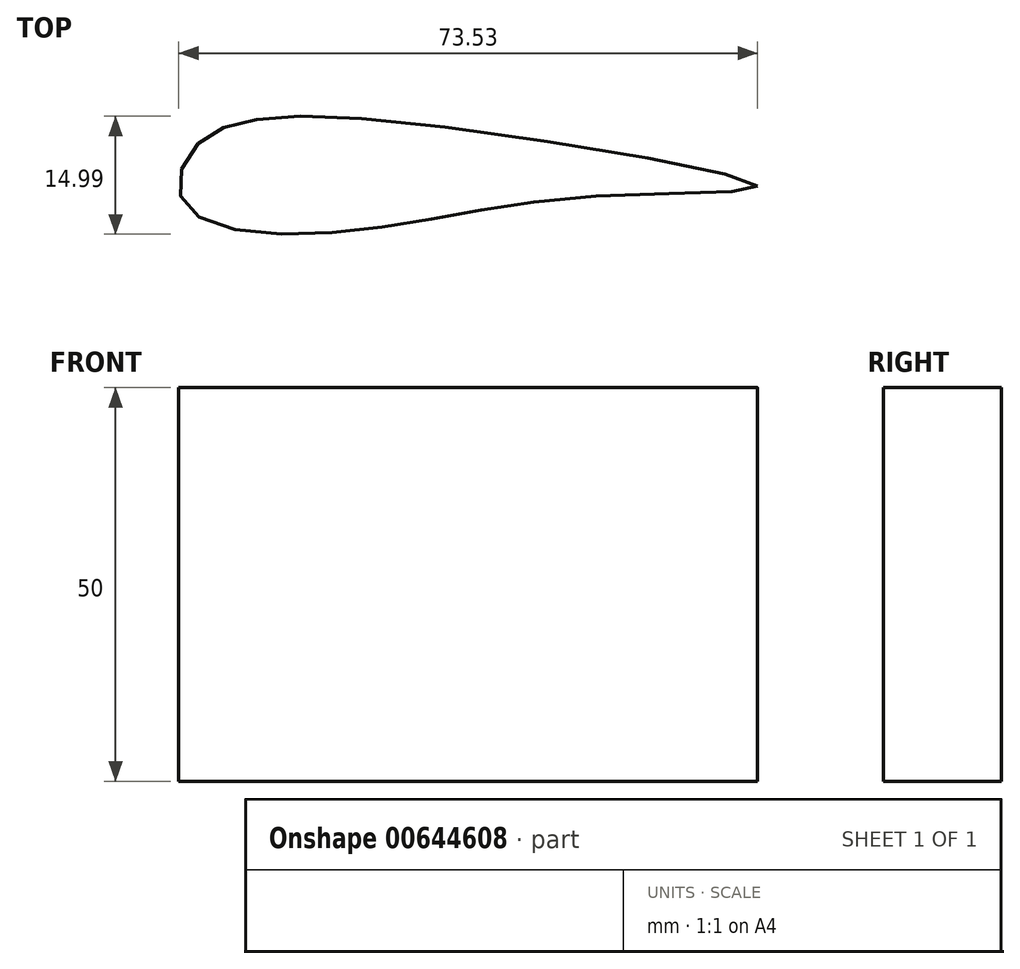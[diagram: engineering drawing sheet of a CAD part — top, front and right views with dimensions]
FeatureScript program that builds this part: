
annotation { "Feature Type Name" : "Feature", "Feature Type Description" : "" }
export const myFeature = defineFeature(function(context is Context, id is Id, definition is map)
    precondition{}
    {
        {
            var Q0;
            Q0=qCreatedBy(makeId("Top.planeOp"),FACE);
            var sketch = newSketch(context, id + "F0", { "sketchPlane" : qUnion([Q0])});
            skFitSpline(sketch, "E0", {"points": [v(73.53, 3.05) * mm, v(29.86, 10.98) * mm, v(8.21, 11.16) * mm, v(2.43, 8.36) * mm, v(0, 3.05) * mm, v(2.73, -1.03) * mm, v(15.6, -3.08) * mm, v(32.77, -1.03) * mm, v(54.14, 1.82) * mm, v(73.53, 3.05) * mm]});
            skSolve(sketch);
        }
        {
            var Q0;
            Q0=qCreatedBy(makeId("Top.planeOp"),FACE);
            cPlane(context, id + "F1", {"entities" : qUnion([Q0]), "cplaneType" : CPlaneType.OFFSET, "offset" : 50 * mm, "width" : 150 * mm, "height" : 150 * mm});
        }
        {
            var Q0;
            Q0 = qSketchRegion(id + "F0", true);
            extrude(context, id + "F2", {"entities" : qUnion([Q0]), "depth" : 50 * mm, "offsetDistance" : 25 * mm});
        }
    });
